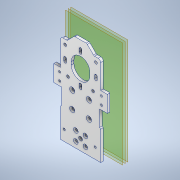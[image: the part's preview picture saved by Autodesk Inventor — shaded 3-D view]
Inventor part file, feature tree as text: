
AUTODESK INVENTOR PART (.ipt)
format: ipt  version: 2020 (Build 240168000, 168)  size: 503,296 bytes
history: native  units: mm
features: sketch x7, hole x7, extrude x5, plane x3, projected_geometry x3, fillet x2, mirror x1, chamfer x1
ambient origin geometry x8: Origin, YZ Plane, XZ Plane, XY Plane, X Axis, Y Axis, Z Axis, Center Point
bodies: Solid1 (feature_tree)
feature tree (29):
  sketch  "Sketch1"  dims[d0=62.0mm d1=22.0mm]
  extrude  "Extrusion1"  Depth=22.0mm
  hole  "Hole1"  [1 undecoded]
  hole  "Hole2"  [1 undecoded]
  hole  "Hole3"  [1 undecoded]
  extrude  "Extrusion2"  Depth=48.0mm
  sketch  "Sketch3"  dims[d5=115.0mm d6=3.175mm d7=0.0mm]
  extrude  "Extrusion3"  Depth=48.0mm
  hole  "Hole4"  [1 undecoded]
  hole  "Hole5"  [1 undecoded]
  plane  "Work Plane1"
  plane  "Work Plane3"
  hole  "Hole6"  [1 undecoded]
  mirror  "Mirror1"
  sketch  "Sketch5"  dims[d10=12.75mm]
  extrude  "Extrusion4"  Depth=3.0mm
  extrude  "Extrusion5"  Depth=48.0mm
  chamfer  "Chamfer1"  Distance=7.0mm
  fillet  "Fillet1"  Radius=12.22mm
  fillet  "Fillet2"  Radius=0.63mm
  hole  "Hole7"  [1 undecoded]
  sketch  "Sketch7"  dims[d18=4.5mm d19=4.5mm d20=4.0mm d21=2.0mm d22=90.0deg d23=8.8mm d24=20.594885mm d25=16.0mm d26=2.9mm d27=4.5mm d28=5.5mm d29=2.0mm d30=90.0deg d31=8.8mm d32=20.594885mm d33=31.0mm d34=31.0mm d35=22.5mm d36=1.7mm d37=3.0mm d38=13.0mm d39=7.0mm d40=12.22mm d41=0.63mm d42=42.0mm d43=8.0mm d45=40.0mm d47=48.0mm d48=0.0mm d49=0.0mm d52=17.0mm d53=35.2mm d54=26.0mm d55=22.25mm d56=3.5mm d57=1.6mm d58=7.0mm d59=13.0mm d60=4.0mm d61=30.0mm d62=12.22mm d63=0.63mm d64=14.0mm d65=4.0mm d66=0.0mm d67=0.0mm d68=3.242mm d69=8.0mm d70=6.3mm d71=2.0mm d72=90.0deg d73=11.8mm d74=20.594885mm d75=20.0mm d76=20.0mm d77=3.2mm d78=8.0mm d79=6.3mm d80=2.0mm d81=90.0deg d82=11.8mm d83=20.594885mm d84=13.0mm d85=6.35mm d86=5.3mm d87=10.0mm d88=19.8mm d89=9.5mm d90=7.0mm d91=1.3mm d92=2.9mm d93=1.8mm d94=12.0mm d95=3.4mm d96=2.459mm d97=6.0mm d98=6.3mm d99=2.0mm d100=90.0deg d101=8.8mm d102=20.594885mm d103=16.75mm d104=1.0mm d107=48.0mm d108=0.0mm d109=0.0mm d110=135.0deg d111=135.0deg d112=15.0mm d113=1.3mm d114=2.0mm d115=45.0deg d116=10.0mm d117=0.0mm d118=3.0mm d119=2.0mm d120=5.615224mm d121=5.615224mm d122=3.242mm d123=8.0mm d124=6.3mm d125=2.0mm d126=90.0deg d127=11.8mm d128=20.594885mm d130=48.0mm d131=37.0mm]
  sketch  "Sketch2"  dims[d2=27.0mm d3=45.4mm]
  plane  "Work Plane2"
  sketch  "Sketch4"  dims[d8=37.0mm d9=19.5mm]
  projected_geometry  "Projected Loop1"
  sketch  "Sketch6"  dims[d11=2.459mm d12=6.0mm d13=4.0mm d14=2.0mm d15=90.0deg d16=8.8mm d17=20.594885mm]
  projected_geometry  "Projected Loop2"
  projected_geometry  "Projected Loop3"
note: 7 required parameter values undecoded (feature->parameter linkage not recoverable at this tier; creation-order binding heuristic only, values carry confidence <= 0.55)
